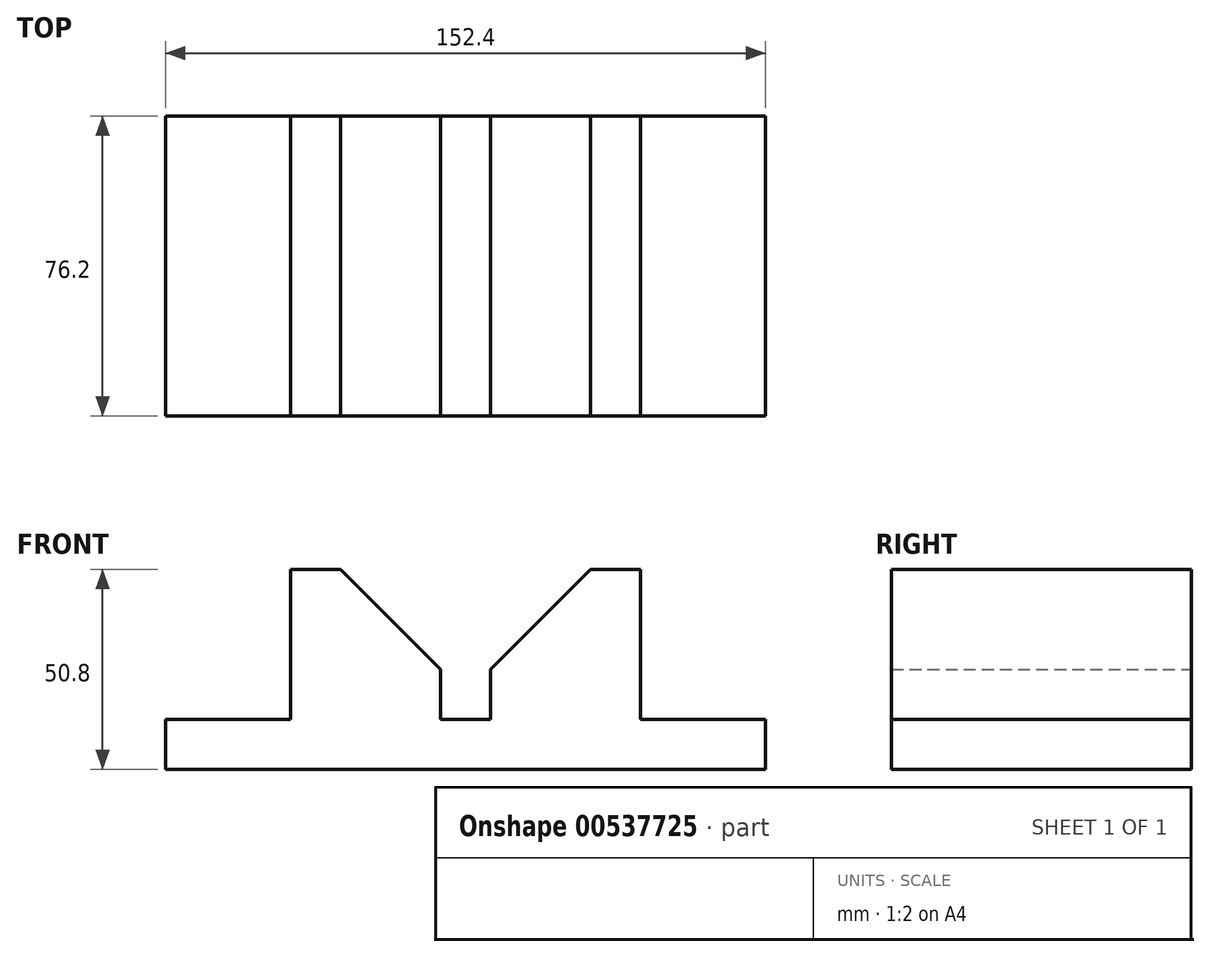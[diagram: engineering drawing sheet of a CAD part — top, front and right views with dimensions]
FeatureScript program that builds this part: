
annotation { "Feature Type Name" : "Feature", "Feature Type Description" : "" }
export const myFeature = defineFeature(function(context is Context, id is Id, definition is map)
    precondition{}
    {
        {
            var Q0;
            Q0=qCreatedBy(makeId("Front.planeOp"),FACE);
            var sketch = newSketch(context, id + "F0", { "sketchPlane" : qUnion([Q0])});
            skLineSegment(sketch, "E0.bottom", {"start": v(-82.53, 1.14) * mm, "end": v(-50.78, 1.14) * mm});
            skLineSegment(sketch, "E0.top", {"start": v(-82.53, -11.56) * mm, "end": v(69.87, -11.56) * mm});
            skLineSegment(sketch, "E0.left", {"start": v(-82.53, 1.14) * mm, "end": v(-82.53, -11.56) * mm});
            skLineSegment(sketch, "E0.right", {"start": v(69.87, 1.14) * mm, "end": v(69.87, -11.56) * mm});
            skLineSegment(sketch, "E1", {"start": v(69.87, 1.14) * mm, "end": v(38.12, 1.14) * mm});
            skLineSegment(sketch, "E2", {"start": v(-50.78, 1.14) * mm, "end": v(-82.53, 1.14) * mm});
            skLineSegment(sketch, "E3", {"start": v(-50.78, 39.24) * mm, "end": v(-50.78, 1.14) * mm});
            skLineSegment(sketch, "E4", {"start": v(38.12, 39.24) * mm, "end": v(38.12, 1.14) * mm});
            skLineSegment(sketch, "E5", {"start": v(-50.78, 39.24) * mm, "end": v(-38.08, 39.24) * mm});
            skLineSegment(sketch, "E6", {"start": v(25.42, 39.24) * mm, "end": v(38.12, 39.24) * mm});
            skLineSegment(sketch, "E7", {"start": v(-12.68, 1.14) * mm, "end": v(-12.68, 13.84) * mm});
            skLineSegment(sketch, "E8", {"start": v(0.02, 1.14) * mm, "end": v(0.02, 13.84) * mm});
            skLineSegment(sketch, "E9", {"start": v(-38.08, 39.24) * mm, "end": v(-12.68, 13.84) * mm});
            skLineSegment(sketch, "E10", {"start": v(0.02, 13.84) * mm, "end": v(25.42, 39.24) * mm});
            skLineSegment(sketch, "E11.trimOffspring", {"start": v(-12.68, 1.14) * mm, "end": v(0.02, 1.14) * mm});
            skLineSegment(sketch, "E12.trimOffspring", {"start": v(38.12, 1.14) * mm, "end": v(69.87, 1.14) * mm});
            skSolve(sketch);
        }
        {
            var Q0;
            Q0=makeQuery(id+"F0.imprint","IMPRINT",FACE,{"disambiguationData":[TD([[makeQuery(id+"F0.imprint","IMPRINT",EDGE,{"derivedFrom":sQuery(id+"F0.wireOp",EDGE,"E0.top")}),1.0]])]});
            extrude(context, id + "F1", {"entities" : qUnion([Q0]), "depth" : 76.2 * mm, "offsetDistance" : 25.4 * mm});
        }
    });
